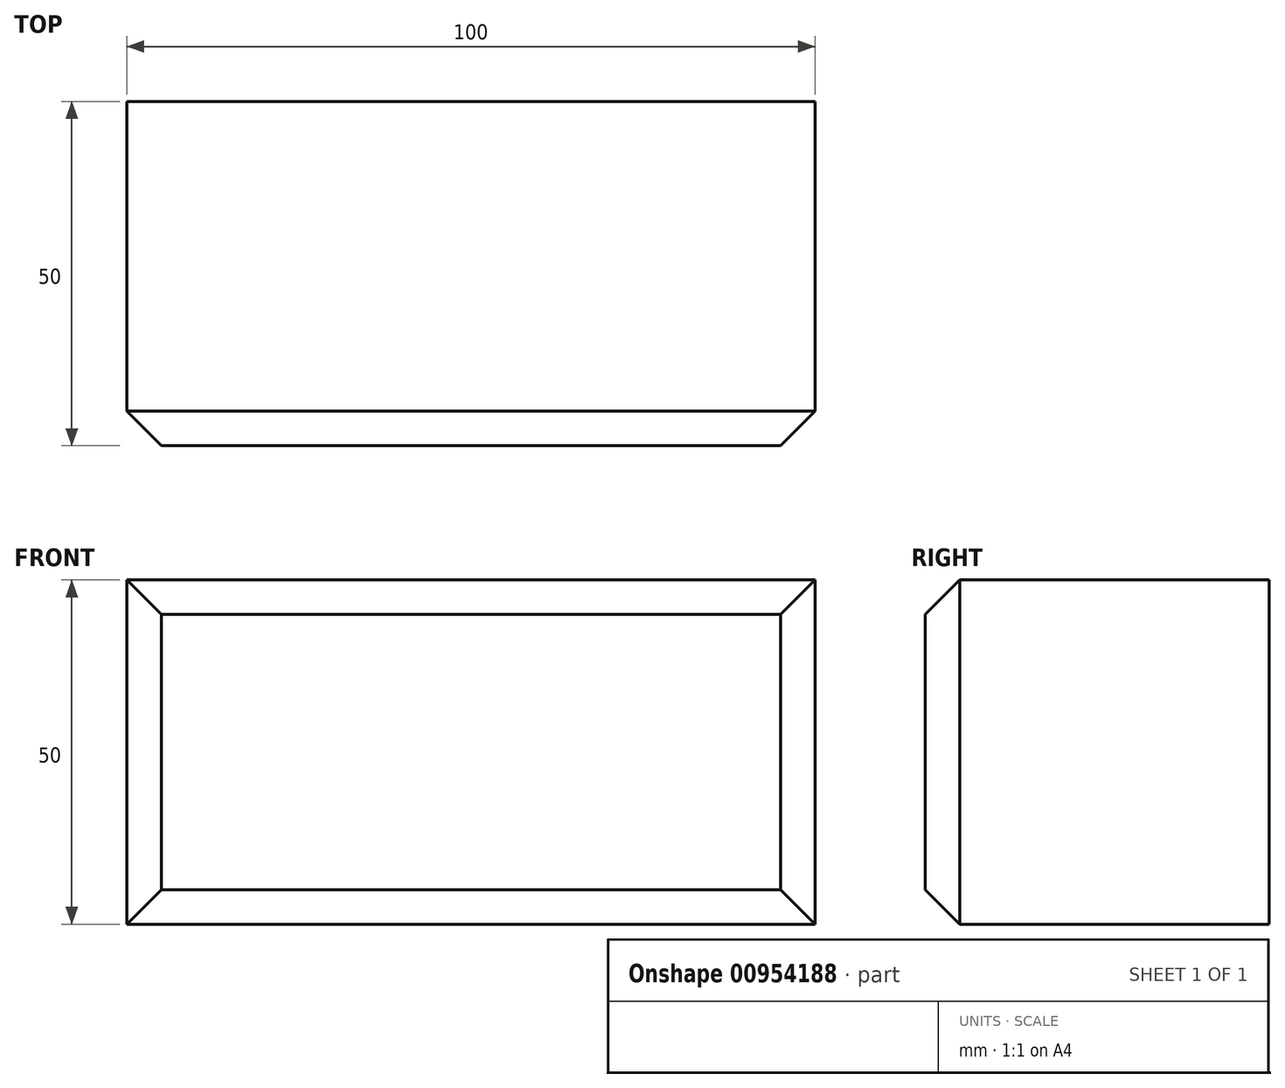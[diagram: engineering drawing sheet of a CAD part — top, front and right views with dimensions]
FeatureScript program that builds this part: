
annotation { "Feature Type Name" : "Feature", "Feature Type Description" : "" }
export const myFeature = defineFeature(function(context is Context, id is Id, definition is map)
    precondition{}
    {
        {
            var Q0;
            Q0=qCreatedBy(makeId("Top.planeOp"),FACE);
            var sketch = newSketch(context, id + "F0", { "sketchPlane" : qUnion([Q0])});
            skLineSegment(sketch, "E0.bottom", {"start": v(-50, 13.22) * mm, "end": v(50, 13.22) * mm});
            skLineSegment(sketch, "E0.top", {"start": v(-50, -36.78) * mm, "end": v(50, -36.78) * mm});
            skLineSegment(sketch, "E0.left", {"start": v(-50, 13.22) * mm, "end": v(-50, -36.78) * mm});
            skLineSegment(sketch, "E0.right", {"start": v(50, 13.22) * mm, "end": v(50, -36.78) * mm});
            skSolve(sketch);
        }
        {
            var Q0;
            Q0=makeQuery(id+"F0.imprint","IMPRINT",FACE,{"disambiguationData":[TD([[makeQuery(id+"F0.imprint","IMPRINT",EDGE,{"derivedFrom":sQuery(id+"F0.wireOp",EDGE,"E0.bottom")}),-1.0]])]});
            extrude(context, id + "F1", {"entities" : qUnion([Q0]), "depth" : 50 * mm, "offsetDistance" : 25 * mm});
        }
        {
            var Q0;
            Q0=makeQuery(id+"F1.opExtrude","SWEPT_EDGE",EDGE,{"disambiguationData":[OSD([sQuery(id+"F0.wireOp",EDGE,"E0.top"),sQuery(id+"F0.wireOp",EDGE,"E0.left")])]});
            var Q1;
            Q1=makeQuery(id+"F1.opExtrude","CAP_EDGE",EDGE,{"disambiguationData":[OSD([sQuery(id+"F0.wireOp",EDGE,"E0.top")])],"isStart":true});
            var Q2;
            Q2=makeQuery(id+"F1.opExtrude","CAP_EDGE",EDGE,{"disambiguationData":[OSD([sQuery(id+"F0.wireOp",EDGE,"E0.top")])],"isStart":false});
            var Q3;
            Q3=makeQuery(id+"F1.opExtrude","SWEPT_EDGE",EDGE,{"disambiguationData":[OSD([sQuery(id+"F0.wireOp",EDGE,"E0.top"),sQuery(id+"F0.wireOp",EDGE,"E0.right")])]});
            chamfer(context, id + "F2", {"entities" : qUnion([Q0, Q1, Q2, Q3]), "width" : 5 * mm, "tangentPropagation" : true});
        }
    });
